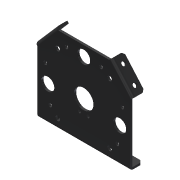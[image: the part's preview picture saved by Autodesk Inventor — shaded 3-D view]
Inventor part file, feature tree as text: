
AUTODESK INVENTOR PART (.ipt)
format: ipt  version: 2013 (Build 170138000, 138)  size: 141,824 bytes
history: native  units: in
note: dims shown in document units (in); Inventor stores cm internally (conversion verified against a paired STEP export)
features: chamfer x1, other x1, imported_body x1
ambient origin geometry x8: Origin, YZ Plane, XZ Plane, XY Plane, X Axis, Y Axis, Z Axis, Center Point
feature tree (3):
  chamfer  "Chamfer1"  [1 undecoded]
  other  "217-2748-001 Rev11"
  imported_body  "Base1"
note: 1 required parameter value undecoded (feature->parameter linkage not recoverable at this tier; creation-order binding heuristic only, values carry confidence <= 0.55)
